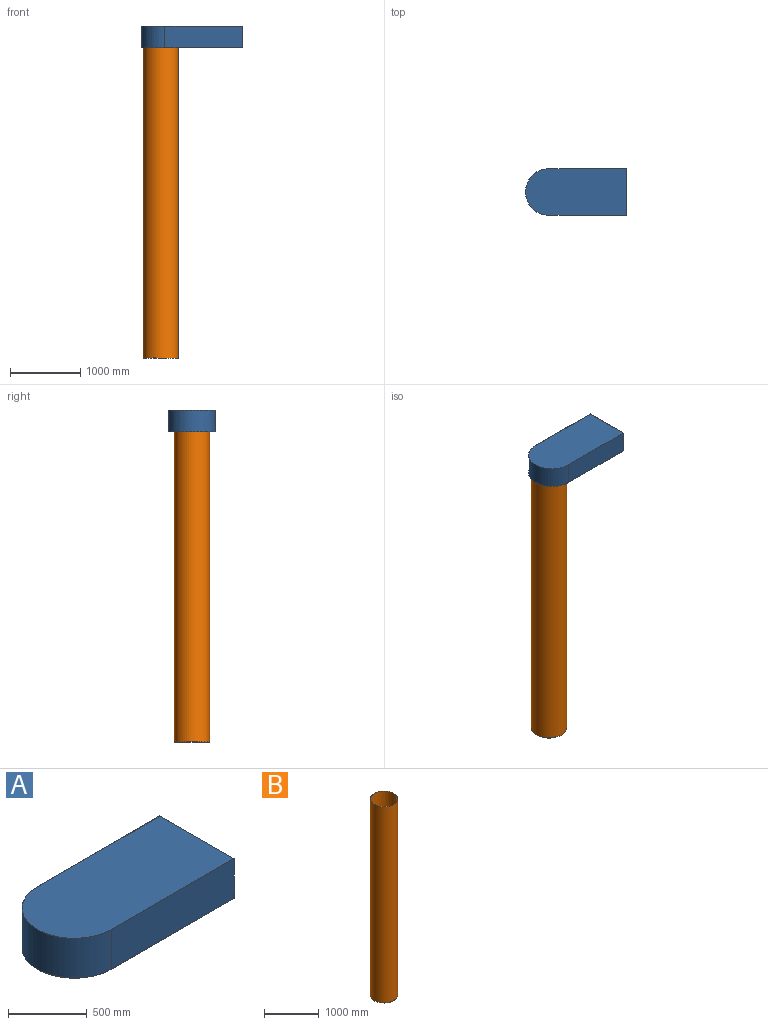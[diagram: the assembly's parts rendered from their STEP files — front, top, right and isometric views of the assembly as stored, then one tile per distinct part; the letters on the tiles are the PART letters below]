
ASSEMBLY  parts=2 mates=1
PART A: 12 faces, bbox 1432x664x310 mm
  f0: plane 664x310mm, normal (1,0,0), area 4845mm2, adj f1,f3,f4,f5,f6,f8,f9,f10
  f1: plane 1100x310mm, normal (0,1,0), area 341000mm2, adj f0,f2,f4,f5
  f2: cylinder r=332mm len=664mm, axis (0,0,1), area 323332.7mm2, adj f1,f3,f4,f5
  f3: plane 1100x310mm, normal (0,-1,0), area 341000mm2, adj f0,f2,f4,f5
  f4: plane 1432x664mm, normal (0,0,-1), area 745620.1mm2, adj f0,f1,f2,f3,f11
  f5: plane 1432x664mm, normal (0,0,1), area 903539.5mm2, adj f0,f1,f2,f3
  f6: plane 1100x305mm, normal (0,-1,0), area 335500mm2, adj f0,f7,f9,f10
  f7: cylinder r=329.5mm len=659mm, axis (0,0,1), area 315722.2mm2, adj f6,f8,f9,f10
  f8: plane 1100x305mm, normal (0,1,0), area 335500mm2, adj f0,f7,f9,f10
  f9: plane 1429.5x659mm, normal (0,0,1), area 731606.8mm2, adj f0,f6,f7,f8,f11
  f10: plane 1429.5x659mm, normal (0,0,-1), area 895441.7mm2, adj f0,f6,f7,f8
  f11: cone r=0mm half-angle=59deg, axis (0,0,1), area 6901.4mm2, adj f4,f9
PART B: 5 faces, bbox 500x500x4400 mm
  f0: cylinder r=250mm len=4400mm, axis (0,0,1), area 6911503.8mm2, adj f1,f2
  f1: plane 500x500mm, normal (0,0,-1), area 196349.5mm2, adj f0
  f2: plane 500x500mm, normal (0,0,1), area 6232.9mm2, adj f0,f3
  f3: cylinder r=246mm len=4396mm, axis (0,0,1), area 6794737.1mm2, adj f2,f4
  f4: plane 492x492mm, normal (0,0,1), area 190116.6mm2, adj f3
PLACE A t=(-363.51,-59.85,39.47)mm
PLACE B t=(-423.51,-59.85,-270.53)mm
MATE revolute B.f0 <-> A.f11  axis (0,0,1) through (-423.51,-59.85,-270.53)mm
